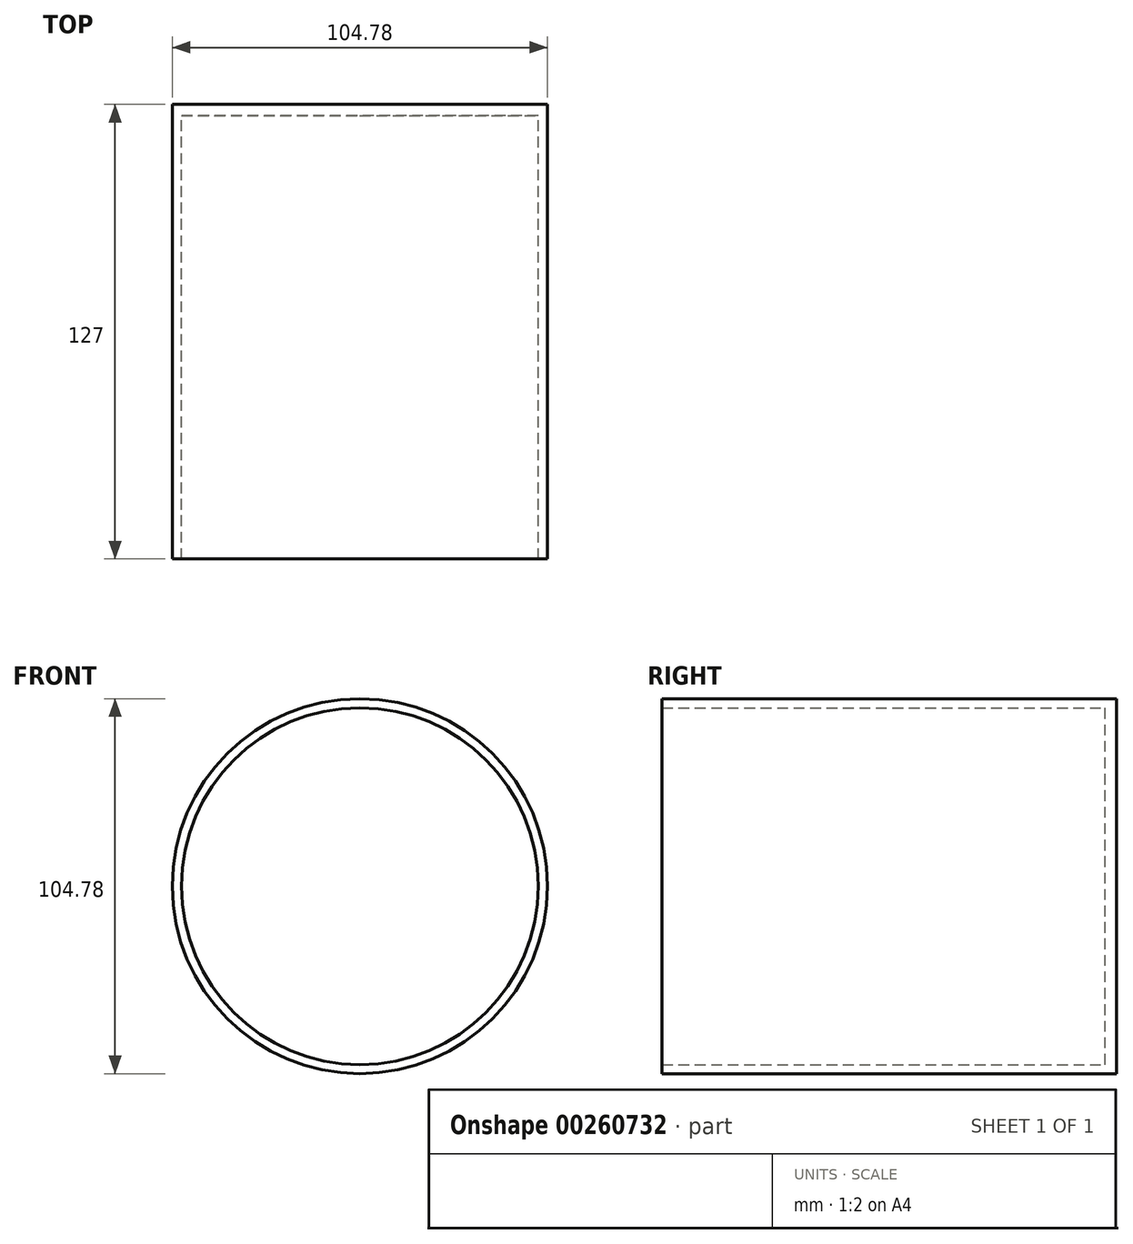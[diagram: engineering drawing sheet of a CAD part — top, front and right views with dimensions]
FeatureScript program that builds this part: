
annotation { "Feature Type Name" : "Feature", "Feature Type Description" : "" }
export const myFeature = defineFeature(function(context is Context, id is Id, definition is map)
    precondition{}
    {
        {
            var Q0;
            Q0=qCreatedBy(makeId("Front.planeOp"),FACE);
            var sketch = newSketch(context, id + "F0", { "sketchPlane" : qUnion([Q0])});
            skCircle(sketch, "E0", {"center": v(0, 0) * mm, "radius": 52.39 * mm});
            skSolve(sketch);
        }
        {
            var Q0;
            Q0=makeQuery(id+"F0.imprint","IMPRINT",FACE,{"disambiguationData":[TD([[makeQuery(id+"F0.imprint","IMPRINT",EDGE,{"derivedFrom":sQuery(id+"F0.wireOp",EDGE,"E0")}),1.0]])]});
            extrude(context, id + "F1", {"entities" : qUnion([Q0]), "depth" : 3.17 * mm});
        }
        {
            var Q0;
            Q0=makeQuery(id+"F1.opExtrude","CAP_FACE",FACE,{"disambiguationData":[OSD([sQuery(id+"F0.wireOp",EDGE,"E0")])],"isStart":false});
            var sketch = newSketch(context, id + "F2", { "sketchPlane" : qUnion([Q0])});
            skCircle(sketch, "E1", {"center": v(0, 0) * mm, "radius": 49.85 * mm});
            skCircle(sketch, "E2", {"center": v(0, 0) * mm, "radius": 52.39 * mm});
            skSolve(sketch);
        }
        {
            var Q0;
            Q0=makeQuery(id+"F2.imprint","IMPRINT",FACE,{"disambiguationData":[TD([[makeQuery(id+"F2.imprint","IMPRINT",EDGE,{"derivedFrom":sQuery(id+"F2.wireOp",EDGE,"E1")}),-1.0]])]});
            extrude(context, id + "F3", {"entities" : qUnion([Q0]), "operationType" : NewBodyOperationType.ADD, "depth" : 123.82 * mm});
        }
    });
